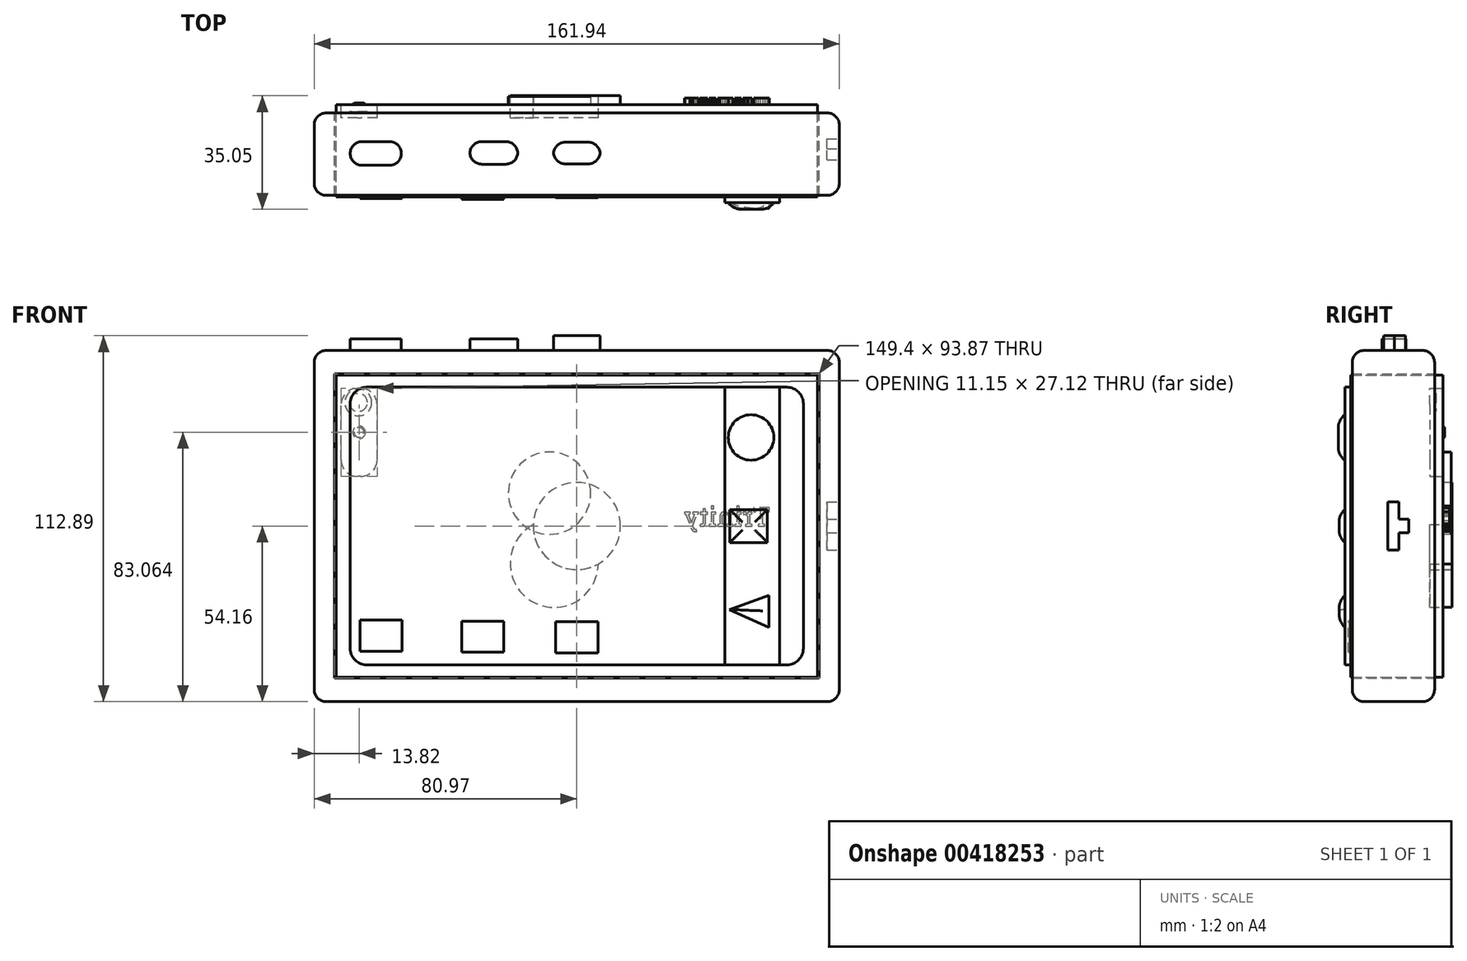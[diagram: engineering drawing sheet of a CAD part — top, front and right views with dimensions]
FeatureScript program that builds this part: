
annotation { "Feature Type Name" : "Feature", "Feature Type Description" : "" }
export const myFeature = defineFeature(function(context is Context, id is Id, definition is map)
    precondition{}
    {
        {
            var Q0;
            Q0=qCreatedBy(makeId("Front.planeOp"),FACE);
            var sketch = newSketch(context, id + "F0", { "sketchPlane" : qUnion([Q0])});
            skLineSegment(sketch, "E0.bottom", {"start": v(-80.97, 54.16) * mm, "end": v(80.97, 54.16) * mm});
            skLineSegment(sketch, "E0.top", {"start": v(-80.97, -54.16) * mm, "end": v(80.97, -54.16) * mm});
            skLineSegment(sketch, "E0.left", {"start": v(-80.97, 54.16) * mm, "end": v(-80.97, -54.16) * mm});
            skLineSegment(sketch, "E0.right", {"start": v(80.97, 54.16) * mm, "end": v(80.97, -54.16) * mm});
            skPoint(sketch, "E0.middle", {"position": v(0, 0) * mm});
            skLineSegment(sketch, "E1.bottom", {"start": v(-74.7, 46.93) * mm, "end": v(74.7, 46.93) * mm});
            skLineSegment(sketch, "E1.top", {"start": v(-74.7, -46.93) * mm, "end": v(74.7, -46.93) * mm});
            skLineSegment(sketch, "E1.left", {"start": v(-74.7, 46.93) * mm, "end": v(-74.7, -46.93) * mm});
            skLineSegment(sketch, "E1.right", {"start": v(74.7, 46.93) * mm, "end": v(74.7, -46.93) * mm});
            skLineSegment(sketch, "E2.bottom", {"start": v(-69.88, 42.84) * mm, "end": v(69.88, 42.84) * mm});
            skLineSegment(sketch, "E2.top", {"start": v(-69.88, -42.84) * mm, "end": v(69.88, -42.84) * mm});
            skLineSegment(sketch, "E2.left", {"start": v(-69.88, 42.84) * mm, "end": v(-69.88, -42.84) * mm});
            skLineSegment(sketch, "E2.right", {"start": v(69.88, 42.84) * mm, "end": v(69.88, -42.84) * mm});
            skSolve(sketch);
        }
        {
            var Q0;
            Q0=makeQuery(id+"F0.imprint","IMPRINT",FACE,{"disambiguationData":[TD([[makeQuery(id+"F0.imprint","IMPRINT",EDGE,{"derivedFrom":sQuery(id+"F0.wireOp",EDGE,"E2.bottom")}),-1.0]])]});
            var Q1;
            Q1=makeQuery(id+"F0.imprint","IMPRINT",FACE,{"disambiguationData":[TD([[makeQuery(id+"F0.imprint","IMPRINT",EDGE,{"derivedFrom":sQuery(id+"F0.wireOp",EDGE,"E0.bottom")}),-1.0]])]});
            extrude(context, id + "F1", {"entities" : qUnion([Q0, Q1]), "depth" : 25.4 * mm});
        }
        {
            var Q0;
            Q0=makeQuery(id+"F1.opExtrude","SWEPT_FACE",FACE,{"disambiguationData":[OSD([sQuery(id+"F0.wireOp",EDGE,"E0.right")])]});
            var Q1;
            Q1=makeQuery(id+"F1.opExtrude","SWEPT_FACE",FACE,{"disambiguationData":[OSD([sQuery(id+"F0.wireOp",EDGE,"E0.bottom")])]});
            var Q2;
            Q2=makeQuery(id+"F1.opExtrude","SWEPT_FACE",FACE,{"disambiguationData":[OSD([sQuery(id+"F0.wireOp",EDGE,"E0.left")])]});
            var Q3;
            Q3=makeQuery(id+"F1.opExtrude","SWEPT_FACE",FACE,{"disambiguationData":[OSD([sQuery(id+"F0.wireOp",EDGE,"E0.top")])]});
            fillet(context, id + "F2", {"entities" : qUnion([Q0, Q1, Q2, Q3]), "radius" : 3.68 * mm, "tangentPropagation" : true, "allowEdgeOverflow" : false});
        }
        {
            var Q0;
            Q0=makeQuery(id+"F1.opExtrude","SWEPT_EDGE",EDGE,{"disambiguationData":[OSD([sQuery(id+"F0.wireOp",EDGE,"E2.bottom"),sQuery(id+"F0.wireOp",EDGE,"E2.left")])]});
            var Q1;
            Q1=makeQuery(id+"F1.opExtrude","SWEPT_EDGE",EDGE,{"disambiguationData":[OSD([sQuery(id+"F0.wireOp",EDGE,"E2.top"),sQuery(id+"F0.wireOp",EDGE,"E2.left")])]});
            var Q2;
            Q2=makeQuery(id+"F1.opExtrude","SWEPT_EDGE",EDGE,{"disambiguationData":[OSD([sQuery(id+"F0.wireOp",EDGE,"E2.top"),sQuery(id+"F0.wireOp",EDGE,"E2.right")])]});
            var Q3;
            Q3=makeQuery(id+"F1.opExtrude","SWEPT_EDGE",EDGE,{"disambiguationData":[OSD([sQuery(id+"F0.wireOp",EDGE,"E2.bottom"),sQuery(id+"F0.wireOp",EDGE,"E2.right")])]});
            fillet(context, id + "F3", {"entities" : qUnion([Q0, Q1, Q2, Q3]), "radius" : 5.08 * mm, "tangentPropagation" : true, "allowEdgeOverflow" : false});
        }
        {
            var Q0;
            Q0=makeQuery(id+"F1.opExtrude","SWEPT_FACE",FACE,{"disambiguationData":[OSD([sQuery(id+"F0.wireOp",EDGE,"E0.bottom")])]});
            var sketch = newSketch(context, id + "F4", { "sketchPlane" : qUnion([Q0])});
            skLineSegment(sketch, "E3", {"start": v(-69.9, -16.15) * mm, "end": v(-54.1, -16.15) * mm});
            skLineSegment(sketch, "E4", {"start": v(-54.1, -16.15) * mm, "end": v(-54.1, -8.85) * mm});
            skLineSegment(sketch, "E5", {"start": v(-54.1, -8.85) * mm, "end": v(-69.9, -8.85) * mm});
            skLineSegment(sketch, "E6", {"start": v(-69.9, -8.85) * mm, "end": v(-69.9, -16.15) * mm});
            skSolve(sketch);
        }
        {
            var Q0;
            Q0=makeQuery(id+"F4.imprint","IMPRINT",FACE,{"disambiguationData":[TD([[makeQuery(id+"F4.imprint","IMPRINT",EDGE,{"derivedFrom":sQuery(id+"F4.wireOp",EDGE,"E3")}),1.0]])]});
            extrude(context, id + "F5", {"entities" : qUnion([Q0]), "operationType" : NewBodyOperationType.ADD, "depth" : 3.56 * mm});
        }
        {
            var Q0;
            Q0=makeQuery(id+"F1.opExtrude","CAP_FACE",FACE,{"disambiguationData":[OSD([sQuery(id+"F0.wireOp",EDGE,"E2.bottom"),sQuery(id+"F0.wireOp",EDGE,"E2.top"),sQuery(id+"F0.wireOp",EDGE,"E2.left"),sQuery(id+"F0.wireOp",EDGE,"E2.right")])],"isStart":true});
            var sketch = newSketch(context, id + "F6", { "sketchPlane" : qUnion([Q0])});
            skLineSegment(sketch, "E7.bottom", {"start": v(74.26, 46.6) * mm, "end": v(-74.26, 46.6) * mm});
            skLineSegment(sketch, "E7.top", {"start": v(74.26, -46.6) * mm, "end": v(-74.26, -46.6) * mm});
            skLineSegment(sketch, "E7.left", {"start": v(74.26, 46.6) * mm, "end": v(74.26, -46.6) * mm});
            skLineSegment(sketch, "E7.right", {"start": v(-74.26, 46.6) * mm, "end": v(-74.26, -46.6) * mm});
            skPoint(sketch, "E7.middle", {"position": v(0, 0) * mm});
            skSolve(sketch);
        }
        {
            var Q0;
            Q0=makeQuery(id+"F6.imprint","IMPRINT",FACE,{"disambiguationData":[TD([[makeQuery(id+"F6.imprint","IMPRINT",EDGE,{"derivedFrom":sQuery(id+"F6.wireOp",EDGE,"E7.bottom")}),1.0]])]});
            extrude(context, id + "F7", {"entities" : qUnion([Q0]), "operationType" : NewBodyOperationType.ADD, "oppositeDirection" : true, "depth" : 25.9 * mm});
        }
        {
            var Q0;
            Q0=makeQuery(id+"F5.opExtrude","SWEPT_EDGE",EDGE,{"disambiguationData":[OSD([sQuery(id+"F4.wireOp",EDGE,"E3"),sQuery(id+"F4.wireOp",EDGE,"E6")])]});
            var Q1;
            Q1=makeQuery(id+"F5.opExtrude","SWEPT_EDGE",EDGE,{"disambiguationData":[OSD([sQuery(id+"F4.wireOp",EDGE,"E5"),sQuery(id+"F4.wireOp",EDGE,"E6")])]});
            var Q2;
            Q2=makeQuery(id+"F5.opExtrude","SWEPT_EDGE",EDGE,{"disambiguationData":[OSD([sQuery(id+"F4.wireOp",EDGE,"E3"),sQuery(id+"F4.wireOp",EDGE,"E4")])]});
            var Q3;
            Q3=makeQuery(id+"F5.opExtrude","SWEPT_EDGE",EDGE,{"disambiguationData":[OSD([sQuery(id+"F4.wireOp",EDGE,"E4"),sQuery(id+"F4.wireOp",EDGE,"E5")])]});
            fillet(context, id + "F8", {"entities" : qUnion([Q0, Q1, Q2, Q3]), "radius" : 3.68 * mm, "tangentPropagation" : true, "allowEdgeOverflow" : false});
        }
        {
            var Q0;
            {var subQ0=sQuery(id+"F0.wireOp",EDGE,"E2.right");var subQ1=sQuery(id+"F0.wireOp",EDGE,"E2.left");var subQ2=sQuery(id+"F0.wireOp",EDGE,"E2.top");var subQ3=sQuery(id+"F0.wireOp",EDGE,"E2.bottom");Q0=makeQuery(id+"F7.boolean.opBoolean","MERGE",FACE,{"derivedFrom":[makeQuery(id+"F1.opExtrude","CAP_FACE",FACE,{"disambiguationData":[OSD([subQ3,subQ2,subQ1,subQ0])],"isStart":true}),makeQuery(id+"F7.opExtrude","CAP_FACE",FACE,{"disambiguationData":[OSD([subQ3,subQ2,subQ1,subQ0,sQuery(id+"F6.wireOp",EDGE,"E7.bottom"),sQuery(id+"F6.wireOp",EDGE,"E7.top"),sQuery(id+"F6.wireOp",EDGE,"E7.left"),sQuery(id+"F6.wireOp",EDGE,"E7.right")])],"isStart":true})]});}
            var sketch = newSketch(context, id + "F9", { "sketchPlane" : qUnion([Q0])});
            skLineSegment(sketch, "E8.bottom", {"start": v(74.26, 46.6) * mm, "end": v(-74.26, 46.6) * mm});
            skLineSegment(sketch, "E8.top", {"start": v(74.26, -46.6) * mm, "end": v(-74.26, -46.6) * mm});
            skLineSegment(sketch, "E8.left", {"start": v(74.26, 46.6) * mm, "end": v(74.26, -46.6) * mm});
            skLineSegment(sketch, "E8.right", {"start": v(-74.26, 46.6) * mm, "end": v(-74.26, -46.6) * mm});
            skPoint(sketch, "E8.middle", {"position": v(0, 0) * mm});
            skSolve(sketch);
        }
        {
            var Q0;
            Q0=makeQuery(id+"F9.imprint","IMPRINT",FACE,{"disambiguationData":[TD([[makeQuery(id+"F9.imprint","IMPRINT",EDGE,{"derivedFrom":sQuery(id+"F9.wireOp",EDGE,"E8.bottom")}),1.0]])]});
            extrude(context, id + "F10", {"entities" : qUnion([Q0]), "depth" : 2.54 * mm});
        }
        {
            var Q0;
            Q0=makeQuery(id+"F1.opExtrude","SWEPT_FACE",FACE,{"disambiguationData":[OSD([sQuery(id+"F0.wireOp",EDGE,"E0.bottom")])]});
            var sketch = newSketch(context, id + "F11", { "sketchPlane" : qUnion([Q0])});
            skLineSegment(sketch, "E9", {"start": v(-62, -12.33) * mm, "end": v(10.84, -12.33) * mm, "construction": true});
            skPoint(sketch, "E9.startSnap0", {"position": v(-62, -16.15) * mm});
            skLineSegment(sketch, "E10", {"start": v(10.84, -12.33) * mm, "end": v(77.28, -12.33) * mm, "construction": true});
            skLineSegment(sketch, "E11.bottom", {"start": v(-32.98, -15.8) * mm, "end": v(-18.19, -15.8) * mm});
            skLineSegment(sketch, "E11.top", {"start": v(-32.98, -8.85) * mm, "end": v(-18.19, -8.85) * mm});
            skLineSegment(sketch, "E11.left", {"start": v(-32.98, -15.8) * mm, "end": v(-32.98, -8.85) * mm});
            skLineSegment(sketch, "E11.right", {"start": v(-18.19, -15.8) * mm, "end": v(-18.19, -8.85) * mm});
            skPoint(sketch, "E11.middle", {"position": v(-25.58, -12.33) * mm});
            skSolve(sketch);
        }
        {
            var Q0;
            Q0=makeQuery(id+"F11.imprint","IMPRINT",FACE,{"disambiguationData":[TD([[makeQuery(id+"F11.imprint","IMPRINT",EDGE,{"derivedFrom":sQuery(id+"F11.wireOp",EDGE,"E11.bottom")}),1.0]])]});
            extrude(context, id + "F12", {"entities" : qUnion([Q0]), "operationType" : NewBodyOperationType.ADD, "depth" : 3.56 * mm});
        }
        {
            var Q0;
            Q0=makeQuery(id+"F12.opExtrude","SWEPT_EDGE",EDGE,{"disambiguationData":[OSD([sQuery(id+"F11.wireOp",EDGE,"E11.bottom"),sQuery(id+"F11.wireOp",EDGE,"E11.left")])]});
            var Q1;
            Q1=makeQuery(id+"F12.opExtrude","SWEPT_EDGE",EDGE,{"disambiguationData":[OSD([sQuery(id+"F11.wireOp",EDGE,"E11.top"),sQuery(id+"F11.wireOp",EDGE,"E11.left")])]});
            var Q2;
            Q2=makeQuery(id+"F12.opExtrude","SWEPT_EDGE",EDGE,{"disambiguationData":[OSD([sQuery(id+"F11.wireOp",EDGE,"E11.bottom"),sQuery(id+"F11.wireOp",EDGE,"E11.right")])]});
            var Q3;
            Q3=makeQuery(id+"F12.opExtrude","SWEPT_EDGE",EDGE,{"disambiguationData":[OSD([sQuery(id+"F11.wireOp",EDGE,"E11.top"),sQuery(id+"F11.wireOp",EDGE,"E11.right")])]});
            fillet(context, id + "F13", {"entities" : qUnion([Q0, Q1, Q2, Q3]), "radius" : 3.68 * mm, "tangentPropagation" : true, "allowEdgeOverflow" : false});
        }
        {
            var Q0;
            Q0=makeQuery(id+"F1.opExtrude","SWEPT_FACE",FACE,{"disambiguationData":[OSD([sQuery(id+"F0.wireOp",EDGE,"E0.bottom")])]});
            var sketch = newSketch(context, id + "F14", { "sketchPlane" : qUnion([Q0])});
            skLineSegment(sketch, "E12", {"start": v(-25.73, -12.36) * mm, "end": v(17.21, -12.36) * mm, "construction": true});
            skLineSegment(sketch, "E13.bottom", {"start": v(-7.2, -15.69) * mm, "end": v(7.2, -15.69) * mm});
            skLineSegment(sketch, "E13.top", {"start": v(-7.2, -9.03) * mm, "end": v(7.2, -9.03) * mm});
            skLineSegment(sketch, "E13.left", {"start": v(-7.2, -15.69) * mm, "end": v(-7.2, -9.03) * mm});
            skLineSegment(sketch, "E13.right", {"start": v(7.2, -15.69) * mm, "end": v(7.2, -9.03) * mm});
            skPoint(sketch, "E13.middle", {"position": v(0, -12.36) * mm});
            skSolve(sketch);
        }
        {
            var Q0;
            Q0=makeQuery(id+"F14.imprint","IMPRINT",FACE,{"disambiguationData":[TD([[makeQuery(id+"F14.imprint","IMPRINT",EDGE,{"derivedFrom":sQuery(id+"F14.wireOp",EDGE,"E13.bottom")}),1.0]])]});
            extrude(context, id + "F15", {"entities" : qUnion([Q0]), "operationType" : NewBodyOperationType.ADD, "depth" : 4.57 * mm});
        }
        {
            var Q0;
            Q0=makeQuery(id+"F15.opExtrude","SWEPT_EDGE",EDGE,{"disambiguationData":[OSD([sQuery(id+"F14.wireOp",EDGE,"E13.bottom"),sQuery(id+"F14.wireOp",EDGE,"E13.right")])]});
            var Q1;
            Q1=makeQuery(id+"F15.opExtrude","SWEPT_EDGE",EDGE,{"disambiguationData":[OSD([sQuery(id+"F14.wireOp",EDGE,"E13.top"),sQuery(id+"F14.wireOp",EDGE,"E13.right")])]});
            var Q2;
            Q2=makeQuery(id+"F15.opExtrude","SWEPT_EDGE",EDGE,{"disambiguationData":[OSD([sQuery(id+"F14.wireOp",EDGE,"E13.bottom"),sQuery(id+"F14.wireOp",EDGE,"E13.left")])]});
            var Q3;
            Q3=makeQuery(id+"F15.opExtrude","SWEPT_EDGE",EDGE,{"disambiguationData":[OSD([sQuery(id+"F14.wireOp",EDGE,"E13.top"),sQuery(id+"F14.wireOp",EDGE,"E13.left")])]});
            fillet(context, id + "F16", {"entities" : qUnion([Q0, Q1, Q2, Q3]), "radius" : 3.68 * mm, "tangentPropagation" : true, "allowEdgeOverflow" : false});
        }
        {
            var Q0;
            Q0=makeQuery(id+"F1.opExtrude","CAP_FACE",FACE,{"disambiguationData":[OSD([sQuery(id+"F0.wireOp",EDGE,"E2.bottom"),sQuery(id+"F0.wireOp",EDGE,"E2.top"),sQuery(id+"F0.wireOp",EDGE,"E2.left"),sQuery(id+"F0.wireOp",EDGE,"E2.right")])],"isStart":false});
            var sketch = newSketch(context, id + "F17", { "sketchPlane" : qUnion([Q0])});
            skLineSegment(sketch, "E14.bottom", {"start": v(-53.84, -29.05) * mm, "end": v(-66.85, -29.05) * mm});
            skLineSegment(sketch, "E14.top", {"start": v(-53.84, -38.68) * mm, "end": v(-66.85, -38.68) * mm});
            skLineSegment(sketch, "E14.left", {"start": v(-53.84, -29.05) * mm, "end": v(-53.84, -38.68) * mm});
            skLineSegment(sketch, "E14.right", {"start": v(-66.85, -29.05) * mm, "end": v(-66.85, -38.68) * mm});
            skPoint(sketch, "E14.middle", {"position": v(-60.35, -33.87) * mm});
            skSolve(sketch);
        }
        {
            var Q0;
            Q0=makeQuery(id+"F17.imprint","IMPRINT",FACE,{"disambiguationData":[TD([[makeQuery(id+"F17.imprint","IMPRINT",EDGE,{"derivedFrom":sQuery(id+"F17.wireOp",EDGE,"E14.bottom")}),1.0]])]});
            extrude(context, id + "F18", {"entities" : qUnion([Q0]), "depth" : 1.02 * mm});
        }
        {
            var Q0;
            Q0=makeQuery(id+"F1.opExtrude","CAP_FACE",FACE,{"disambiguationData":[OSD([sQuery(id+"F0.wireOp",EDGE,"E2.bottom"),sQuery(id+"F0.wireOp",EDGE,"E2.top"),sQuery(id+"F0.wireOp",EDGE,"E2.left"),sQuery(id+"F0.wireOp",EDGE,"E2.right")])],"isStart":false});
            var sketch = newSketch(context, id + "F19", { "sketchPlane" : qUnion([Q0])});
            skLineSegment(sketch, "E15", {"start": v(-62.3, -34.14) * mm, "end": v(15.58, -34.14) * mm, "construction": true});
            skLineSegment(sketch, "E16.bottom", {"start": v(-35.48, -38.96) * mm, "end": v(-22.47, -38.96) * mm});
            skLineSegment(sketch, "E16.top", {"start": v(-35.48, -29.32) * mm, "end": v(-22.47, -29.32) * mm});
            skLineSegment(sketch, "E16.left", {"start": v(-35.48, -38.96) * mm, "end": v(-35.48, -29.32) * mm});
            skLineSegment(sketch, "E16.right", {"start": v(-22.47, -38.96) * mm, "end": v(-22.47, -29.32) * mm});
            skPoint(sketch, "E16.middle", {"position": v(-28.98, -34.14) * mm});
            skSolve(sketch);
        }
        {
            var Q0;
            Q0=makeQuery(id+"F19.imprint","IMPRINT",FACE,{"disambiguationData":[TD([[makeQuery(id+"F19.imprint","IMPRINT",EDGE,{"derivedFrom":sQuery(id+"F19.wireOp",EDGE,"E16.bottom")}),1.0]])]});
            extrude(context, id + "F20", {"entities" : qUnion([Q0]), "depth" : 1.27 * mm});
        }
        {
            var Q0;
            Q0=makeQuery(id+"F1.opExtrude","CAP_FACE",FACE,{"disambiguationData":[OSD([sQuery(id+"F0.wireOp",EDGE,"E2.bottom"),sQuery(id+"F0.wireOp",EDGE,"E2.top"),sQuery(id+"F0.wireOp",EDGE,"E2.left"),sQuery(id+"F0.wireOp",EDGE,"E2.right")])],"isStart":false});
            var sketch = newSketch(context, id + "F21", { "sketchPlane" : qUnion([Q0])});
            skLineSegment(sketch, "E17", {"start": v(-28.88, -34.33) * mm, "end": v(69.88, -34.33) * mm, "construction": true});
            skLineSegment(sketch, "E18.bottom", {"start": v(-6.5, -39.15) * mm, "end": v(6.5, -39.15) * mm});
            skLineSegment(sketch, "E18.top", {"start": v(-6.5, -29.5) * mm, "end": v(6.5, -29.5) * mm});
            skLineSegment(sketch, "E18.left", {"start": v(-6.5, -39.15) * mm, "end": v(-6.5, -29.5) * mm});
            skLineSegment(sketch, "E18.right", {"start": v(6.5, -39.15) * mm, "end": v(6.5, -29.5) * mm});
            skPoint(sketch, "E18.middle", {"position": v(0, -34.33) * mm});
            skSolve(sketch);
        }
        {
            var Q0;
            Q0=makeQuery(id+"F21.imprint","IMPRINT",FACE,{"disambiguationData":[TD([[makeQuery(id+"F21.imprint","IMPRINT",EDGE,{"derivedFrom":sQuery(id+"F21.wireOp",EDGE,"E18.bottom")}),1.0]])]});
            extrude(context, id + "F22", {"entities" : qUnion([Q0]), "depth" : 0.76 * mm});
        }
        {
            var Q0;
            Q0=makeQuery(id+"F1.opExtrude","CAP_FACE",FACE,{"disambiguationData":[OSD([sQuery(id+"F0.wireOp",EDGE,"E2.bottom"),sQuery(id+"F0.wireOp",EDGE,"E2.top"),sQuery(id+"F0.wireOp",EDGE,"E2.left"),sQuery(id+"F0.wireOp",EDGE,"E2.right")])],"isStart":false});
            var sketch = newSketch(context, id + "F23", { "sketchPlane" : qUnion([Q0])});
            skLineSegment(sketch, "E19.bottom", {"start": v(45.66, -42.84) * mm, "end": v(62.53, -42.84) * mm});
            skLineSegment(sketch, "E19.top", {"start": v(45.66, 42.84) * mm, "end": v(62.53, 42.84) * mm});
            skLineSegment(sketch, "E19.left", {"start": v(45.66, -42.84) * mm, "end": v(45.66, 42.84) * mm});
            skLineSegment(sketch, "E19.right", {"start": v(62.53, -42.84) * mm, "end": v(62.53, 42.84) * mm});
            skPoint(sketch, "E19.middle", {"position": v(54.1, 0) * mm});
            skSolve(sketch);
        }
        {
            var Q0;
            Q0=makeQuery(id+"F23.imprint","IMPRINT",FACE,{"disambiguationData":[TD([[makeQuery(id+"F23.imprint","IMPRINT",EDGE,{"derivedFrom":sQuery(id+"F23.wireOp",EDGE,"E19.bottom")}),1.0]])]});
            extrude(context, id + "F24", {"entities" : qUnion([Q0]), "depth" : 2.3 * mm});
        }
        {
            var Q0;
            Q0=makeQuery(id+"F24.opExtrude","CAP_FACE",FACE,{"disambiguationData":[OSD([sQuery(id+"F23.wireOp",EDGE,"E19.bottom"),sQuery(id+"F23.wireOp",EDGE,"E19.top"),sQuery(id+"F23.wireOp",EDGE,"E19.left"),sQuery(id+"F23.wireOp",EDGE,"E19.right")])],"isStart":false});
            var sketch = newSketch(context, id + "F25", { "sketchPlane" : qUnion([Q0])});
            skLineSegment(sketch, "E20.bottom", {"start": v(58.8, 5.06) * mm, "end": v(47.23, 5.06) * mm});
            skLineSegment(sketch, "E20.top", {"start": v(58.8, -5.06) * mm, "end": v(47.23, -5.06) * mm});
            skLineSegment(sketch, "E20.left", {"start": v(58.8, 5.06) * mm, "end": v(58.8, -5.06) * mm});
            skLineSegment(sketch, "E20.right", {"start": v(47.23, 5.06) * mm, "end": v(47.23, -5.06) * mm});
            skPoint(sketch, "E20.middle", {"position": v(53.01, 0) * mm});
            skSolve(sketch);
        }
        {
            var Q0;
            Q0=makeQuery(id+"F25.imprint","IMPRINT",FACE,{"disambiguationData":[TD([[makeQuery(id+"F25.imprint","IMPRINT",EDGE,{"derivedFrom":sQuery(id+"F25.wireOp",EDGE,"E20.bottom")}),1.0]])]});
            extrude(context, id + "F26", {"entities" : qUnion([Q0]), "depth" : 1.78 * mm});
        }
        {
            var Q0;
            Q0=makeQuery(id+"F24.opExtrude","CAP_FACE",FACE,{"disambiguationData":[OSD([sQuery(id+"F23.wireOp",EDGE,"E19.bottom"),sQuery(id+"F23.wireOp",EDGE,"E19.top"),sQuery(id+"F23.wireOp",EDGE,"E19.left"),sQuery(id+"F23.wireOp",EDGE,"E19.right")])],"isStart":false});
            var sketch = newSketch(context, id + "F27", { "sketchPlane" : qUnion([Q0])});
            skLineSegment(sketch, "E21", {"start": v(53.75, 0) * mm, "end": v(53.75, -42.84) * mm, "construction": true});
            skPoint(sketch, "E21.startSnap0", {"position": v(62.53, 0) * mm});
            skLineSegment(sketch, "E22", {"start": v(53.75, 0) * mm, "end": v(53.75, 42.84) * mm, "construction": true});
            skCircle(sketch, "E23", {"center": v(53.75, 27.32) * mm, "radius": 7.02 * mm});
            skSolve(sketch);
        }
        {
            var Q0;
            Q0=makeQuery(id+"F27.imprint","IMPRINT",FACE,{"disambiguationData":[TD([[makeQuery(id+"F27.imprint","IMPRINT",EDGE,{"derivedFrom":sQuery(id+"F27.wireOp",EDGE,"E23")}),1.0]])]});
            extrude(context, id + "F28", {"entities" : qUnion([Q0]), "depth" : 2.03 * mm});
        }
        {
            var Q0;
            Q0=makeQuery(id+"F24.opExtrude","CAP_FACE",FACE,{"disambiguationData":[OSD([sQuery(id+"F23.wireOp",EDGE,"E19.bottom"),sQuery(id+"F23.wireOp",EDGE,"E19.top"),sQuery(id+"F23.wireOp",EDGE,"E19.left"),sQuery(id+"F23.wireOp",EDGE,"E19.right")])],"isStart":false});
            var sketch = newSketch(context, id + "F29", { "sketchPlane" : qUnion([Q0])});
            skLineSegment(sketch, "E24", {"start": v(53.96, 0) * mm, "end": v(53.96, -42.84) * mm, "construction": true});
            skLineSegment(sketch, "E25", {"start": v(47.07, -25.76) * mm, "end": v(59.23, -21.42) * mm});
            skPoint(sketch, "E25.endSnap0", {"position": v(53.96, -21.42) * mm});
            skLineSegment(sketch, "E26", {"start": v(59.23, -21.42) * mm, "end": v(59.23, -31.23) * mm});
            skLineSegment(sketch, "E27", {"start": v(59.23, -31.23) * mm, "end": v(47.07, -25.76) * mm});
            skSolve(sketch);
        }
        {
            var Q0;
            Q0=makeQuery(id+"F29.imprint","IMPRINT",FACE,{"disambiguationData":[TD([[makeQuery(id+"F29.imprint","IMPRINT",EDGE,{"derivedFrom":sQuery(id+"F29.wireOp",EDGE,"E25")}),-1.0]])]});
            extrude(context, id + "F30", {"entities" : qUnion([Q0]), "depth" : 1.78 * mm});
        }
        {
            var Q0;
            Q0=makeQuery(id+"F10.opExtrude","CAP_FACE",FACE,{"disambiguationData":[OSD([sQuery(id+"F9.wireOp",EDGE,"E8.bottom"),sQuery(id+"F9.wireOp",EDGE,"E8.top"),sQuery(id+"F9.wireOp",EDGE,"E8.left"),sQuery(id+"F9.wireOp",EDGE,"E8.right")])],"isStart":false});
            var sketch = newSketch(context, id + "F31", { "sketchPlane" : qUnion([Q0])});
            skCircle(sketch, "E28", {"center": v(0, 0) * mm, "radius": 13.44 * mm});
            skSolve(sketch);
        }
        {
            var Q0;
            Q0=makeQuery(id+"F31.imprint","IMPRINT",FACE,{"disambiguationData":[TD([[makeQuery(id+"F31.imprint","IMPRINT",EDGE,{"derivedFrom":sQuery(id+"F31.wireOp",EDGE,"E28")}),1.0]])]});
            extrude(context, id + "F32", {"entities" : qUnion([Q0]), "depth" : 2.8 * mm});
        }
        {
            var Q0;
            Q0=makeQuery(id+"F10.opExtrude","CAP_FACE",FACE,{"disambiguationData":[OSD([sQuery(id+"F9.wireOp",EDGE,"E8.bottom"),sQuery(id+"F9.wireOp",EDGE,"E8.top"),sQuery(id+"F9.wireOp",EDGE,"E8.left"),sQuery(id+"F9.wireOp",EDGE,"E8.right")])],"isStart":false});
            var sketch = newSketch(context, id + "F33", { "sketchPlane" : qUnion([Q0])});
            skCircle(sketch, "E29", {"center": v(8.4, 10.13) * mm, "radius": 12.7 * mm});
            skSolve(sketch);
        }
        {
            var Q0;
            Q0=makeQuery(id+"F33.imprint","IMPRINT",FACE,{"disambiguationData":[TD([[makeQuery(id+"F33.imprint","IMPRINT",EDGE,{"derivedFrom":sQuery(id+"F33.wireOp",EDGE,"E29")}),1.0]])]});
            extrude(context, id + "F34", {"entities" : qUnion([Q0]), "depth" : 2.54 * mm});
        }
        {
            var Q0;
            Q0=makeQuery(id+"F32.opExtrude","CAP_FACE",FACE,{"disambiguationData":[OSD([sQuery(id+"F31.wireOp",EDGE,"E28")])],"isStart":false});
            var sketch = newSketch(context, id + "F35", { "sketchPlane" : qUnion([Q0])});
            skCircle(sketch, "E30", {"center": v(6.96, -11.5) * mm, "radius": 13.6 * mm});
            skSolve(sketch);
        }
        {
            var Q0;
            {var subQ0=sQuery(id+"F35.wireOp",EDGE,"E30");var subQ1=makeQuery(id+"F32.opExtrude","CAP_EDGE",EDGE,{"disambiguationData":[OSD([sQuery(id+"F31.wireOp",EDGE,"E28")])],"isStart":false});var subQ2=makeQuery(id+"F35.imprint","INTERSECT",VERTEX,{"disambiguationData":[OD(0.0)],"derivedFrom":[subQ1,subQ0]});Q0=makeQuery(id+"F35.imprint","IMPRINT",FACE,{"disambiguationData":[TD([[makeQuery(id+"F35.imprint","IMPRINT",EDGE,{"disambiguationData":[TD([[subQ2,1.0]])],"derivedFrom":subQ0}),1.0]])]});}
            extrude(context, id + "F36", {"entities" : qUnion([Q0]), "oppositeDirection" : true, "depth" : 6.86 * mm});
        }
        {
            var Q0;
            Q0=makeQuery(id+"F10.opExtrude","CAP_FACE",FACE,{"disambiguationData":[OSD([sQuery(id+"F9.wireOp",EDGE,"E8.bottom"),sQuery(id+"F9.wireOp",EDGE,"E8.top"),sQuery(id+"F9.wireOp",EDGE,"E8.left"),sQuery(id+"F9.wireOp",EDGE,"E8.right")])],"isStart":false});
            var sketch = newSketch(context, id + "F37", { "sketchPlane" : qUnion([Q0])});
            skText(sketch, "E31", { "text": "Trinity", "fontName": "RobotoSlab-Regular.ttf"});
            const initialGuessF37  = {"E31": [-0.05947, 0, 1, 0, 0.0058]};
            skSetInitialGuess(sketch, initialGuessF37);
            skSolve(sketch);
        }
        {
            var Q0;
            Q0 = qSketchRegion(id + "F37", true);
            extrude(context, id + "F38", {"entities" : qUnion([Q0]), "depth" : 2.03 * mm});
        }
        {
            var Q0;
            Q0=makeQuery(id+"F30.opExtrude","CAP_EDGE",EDGE,{"disambiguationData":[OSD([sQuery(id+"F29.wireOp",EDGE,"E27")])],"isStart":false});
            var Q1;
            Q1=makeQuery(id+"F30.opExtrude","CAP_EDGE",EDGE,{"disambiguationData":[OSD([sQuery(id+"F29.wireOp",EDGE,"E25")])],"isStart":false});
            var Q2;
            Q2=makeQuery(id+"F26.opExtrude","CAP_EDGE",EDGE,{"disambiguationData":[OSD([sQuery(id+"F25.wireOp",EDGE,"E20.right")])],"isStart":false});
            var Q3;
            Q3=makeQuery(id+"F26.opExtrude","CAP_EDGE",EDGE,{"disambiguationData":[OSD([sQuery(id+"F25.wireOp",EDGE,"E20.bottom")])],"isStart":false});
            var Q4;
            Q4=makeQuery(id+"F26.opExtrude","CAP_EDGE",EDGE,{"disambiguationData":[OSD([sQuery(id+"F25.wireOp",EDGE,"E20.left")])],"isStart":false});
            var Q5;
            Q5=makeQuery(id+"F26.opExtrude","CAP_EDGE",EDGE,{"disambiguationData":[OSD([sQuery(id+"F25.wireOp",EDGE,"E20.top")])],"isStart":false});
            var Q6;
            Q6=makeQuery(id+"F28.opExtrude","CAP_FACE",FACE,{"disambiguationData":[OSD([sQuery(id+"F27.wireOp",EDGE,"E23")])],"isStart":false});
            fillet(context, id + "F39", {"entities" : qUnion([Q0, Q1, Q2, Q3, Q4, Q5, Q6]), "radius" : 5.08 * mm, "tangentPropagation" : true, "allowEdgeOverflow" : false});
        }
        {
            var Q0;
            Q0=makeQuery(id+"F1.opExtrude","SWEPT_FACE",FACE,{"disambiguationData":[OSD([sQuery(id+"F0.wireOp",EDGE,"E0.right")])]});
            var sketch = newSketch(context, id + "F40", { "sketchPlane" : qUnion([Q0])});
            skLineSegment(sketch, "E32", {"start": v(-21.72, 0) * mm, "end": v(0, 0) * mm, "construction": true});
            skLineSegment(sketch, "E33", {"start": v(-14.5, 0) * mm, "end": v(-14.5, -7.44) * mm});
            skLineSegment(sketch, "E34", {"start": v(-14.5, -7.44) * mm, "end": v(-11.01, -7.44) * mm});
            skLineSegment(sketch, "E35", {"start": v(-11.01, -7.44) * mm, "end": v(-11.01, -2.11) * mm});
            skLineSegment(sketch, "E36", {"start": v(-11.01, -2.11) * mm, "end": v(-7.94, -2.11) * mm});
            skLineSegment(sketch, "E37", {"start": v(-7.94, -2.11) * mm, "end": v(-7.94, 2.11) * mm});
            skLineSegment(sketch, "E38", {"start": v(-7.94, 2.11) * mm, "end": v(-11.01, 2.11) * mm});
            skLineSegment(sketch, "E39", {"start": v(-11.01, 2.11) * mm, "end": v(-11.01, 7.44) * mm});
            skLineSegment(sketch, "E40", {"start": v(-11.01, 7.44) * mm, "end": v(-14.5, 7.44) * mm});
            skLineSegment(sketch, "E41", {"start": v(-14.5, 7.44) * mm, "end": v(-14.5, 0) * mm});
            skSolve(sketch);
        }
        {
            var Q0;
            Q0=makeQuery(id+"F40.imprint","IMPRINT",FACE,{"disambiguationData":[TD([[makeQuery(id+"F40.imprint","IMPRINT",EDGE,{"derivedFrom":sQuery(id+"F40.wireOp",EDGE,"E33")}),1.0]])]});
            extrude(context, id + "F41", {"entities" : qUnion([Q0]), "operationType" : NewBodyOperationType.REMOVE, "oppositeDirection" : true, "depth" : 3.8 * mm});
        }
        {
            var Q0;
            Q0=makeQuery(id+"F10.opExtrude","CAP_FACE",FACE,{"disambiguationData":[OSD([sQuery(id+"F9.wireOp",EDGE,"E8.bottom"),sQuery(id+"F9.wireOp",EDGE,"E8.top"),sQuery(id+"F9.wireOp",EDGE,"E8.left"),sQuery(id+"F9.wireOp",EDGE,"E8.right")])],"isStart":false});
            var sketch = newSketch(context, id + "F42", { "sketchPlane" : qUnion([Q0])});
            skLineSegment(sketch, "E42.bottom", {"start": v(72.73, 42.46) * mm, "end": v(61.57, 42.46) * mm});
            skLineSegment(sketch, "E42.top", {"start": v(72.73, 15.34) * mm, "end": v(61.57, 15.34) * mm});
            skLineSegment(sketch, "E42.left", {"start": v(72.73, 42.46) * mm, "end": v(72.73, 15.34) * mm});
            skLineSegment(sketch, "E42.right", {"start": v(61.57, 42.46) * mm, "end": v(61.57, 15.34) * mm});
            skSolve(sketch);
        }
        {
            var Q0;
            Q0=makeQuery(id+"F42.imprint","IMPRINT",FACE,{"disambiguationData":[TD([[makeQuery(id+"F42.imprint","IMPRINT",EDGE,{"derivedFrom":sQuery(id+"F42.wireOp",EDGE,"E42.bottom")}),1.0]])]});
            extrude(context, id + "F43", {"entities" : qUnion([Q0]), "operationType" : NewBodyOperationType.REMOVE, "oppositeDirection" : true, "depth" : 4.06 * mm});
        }
        {
            var Q0;
            Q0=makeQuery(id+"F43.boolean.opBoolean","COPY",EDGE,{"derivedFrom":makeQuery(id+"F43.opExtrude","SWEPT_EDGE",EDGE,{"disambiguationData":[OSD([sQuery(id+"F42.wireOp",EDGE,"E42.bottom"),sQuery(id+"F42.wireOp",EDGE,"E42.left")])]})});
            var Q1;
            Q1=makeQuery(id+"F43.boolean.opBoolean","COPY",EDGE,{"derivedFrom":makeQuery(id+"F43.opExtrude","SWEPT_EDGE",EDGE,{"disambiguationData":[OSD([sQuery(id+"F42.wireOp",EDGE,"E42.bottom"),sQuery(id+"F42.wireOp",EDGE,"E42.right")])]})});
            var Q2;
            Q2=makeQuery(id+"F43.boolean.opBoolean","COPY",EDGE,{"derivedFrom":makeQuery(id+"F43.opExtrude","SWEPT_EDGE",EDGE,{"disambiguationData":[OSD([sQuery(id+"F42.wireOp",EDGE,"E42.top"),sQuery(id+"F42.wireOp",EDGE,"E42.left")])]})});
            var Q3;
            Q3=makeQuery(id+"F43.boolean.opBoolean","COPY",EDGE,{"derivedFrom":makeQuery(id+"F43.opExtrude","SWEPT_EDGE",EDGE,{"disambiguationData":[OSD([sQuery(id+"F42.wireOp",EDGE,"E42.top"),sQuery(id+"F42.wireOp",EDGE,"E42.right")])]})});
            fillet(context, id + "F44", {"entities" : qUnion([Q0, Q1, Q2, Q3]), "radius" : 5.08 * mm, "tangentPropagation" : true, "allowEdgeOverflow" : false});
        }
        {
            var Q0;
            {var subQ0=sQuery(id+"F0.wireOp",EDGE,"E2.right");var subQ1=sQuery(id+"F0.wireOp",EDGE,"E2.left");var subQ2=sQuery(id+"F0.wireOp",EDGE,"E2.top");var subQ3=sQuery(id+"F0.wireOp",EDGE,"E2.bottom");Q0=makeQuery(id+"F7.boolean.opBoolean","MERGE",FACE,{"derivedFrom":[makeQuery(id+"F1.opExtrude","CAP_FACE",FACE,{"disambiguationData":[OSD([subQ3,subQ2,subQ1,subQ0])],"isStart":true}),makeQuery(id+"F7.opExtrude","CAP_FACE",FACE,{"disambiguationData":[OSD([subQ3,subQ2,subQ1,subQ0,sQuery(id+"F6.wireOp",EDGE,"E7.bottom"),sQuery(id+"F6.wireOp",EDGE,"E7.top"),sQuery(id+"F6.wireOp",EDGE,"E7.left"),sQuery(id+"F6.wireOp",EDGE,"E7.right")])],"isStart":true})]});}
            var sketch = newSketch(context, id + "F45", { "sketchPlane" : qUnion([Q0])});
            skCircle(sketch, "E43", {"center": v(67.4, 38.13) * mm, "radius": 4.15 * mm});
            skSolve(sketch);
        }
        {
            var Q0;
            Q0=makeQuery(id+"F45.imprint","IMPRINT",FACE,{"disambiguationData":[TD([[makeQuery(id+"F45.imprint","IMPRINT",EDGE,{"derivedFrom":sQuery(id+"F45.wireOp",EDGE,"E43")}),1.0]])]});
            extrude(context, id + "F46", {"entities" : qUnion([Q0]), "depth" : 0.15 * mm});
        }
        {
            var Q0;
            Q0=makeQuery(id+"F46.opExtrude","CAP_FACE",FACE,{"disambiguationData":[OSD([sQuery(id+"F45.wireOp",EDGE,"E43")])],"isStart":false});
            var sketch = newSketch(context, id + "F47", { "sketchPlane" : qUnion([Q0])});
            skCircle(sketch, "E44", {"center": v(67.4, 38.13) * mm, "radius": 2.8 * mm});
            skSolve(sketch);
        }
        {
            var Q0;
            Q0=makeQuery(id+"F47.imprint","IMPRINT",FACE,{"disambiguationData":[TD([[makeQuery(id+"F47.imprint","IMPRINT",EDGE,{"derivedFrom":sQuery(id+"F47.wireOp",EDGE,"E44")}),1.0]])]});
            extrude(context, id + "F48", {"entities" : qUnion([Q0]), "depth" : 0.25 * mm});
        }
        {
            var Q0;
            Q0=makeQuery(id+"F10.opExtrude","CAP_FACE",FACE,{"disambiguationData":[OSD([sQuery(id+"F9.wireOp",EDGE,"E8.bottom"),sQuery(id+"F9.wireOp",EDGE,"E8.top"),sQuery(id+"F9.wireOp",EDGE,"E8.left"),sQuery(id+"F9.wireOp",EDGE,"E8.right")])],"isStart":false});
            var sketch = newSketch(context, id + "F49", { "sketchPlane" : qUnion([Q0])});
            skLineSegment(sketch, "E45", {"start": v(61.57, 28.9) * mm, "end": v(72.73, 28.9) * mm, "construction": true});
            skCircle(sketch, "E46", {"center": v(67.15, 28.9) * mm, "radius": 1.94 * mm});
            skSolve(sketch);
        }
        {
            var Q0;
            Q0=makeQuery(id+"F49.imprint","IMPRINT",FACE,{"disambiguationData":[TD([[makeQuery(id+"F49.imprint","IMPRINT",EDGE,{"derivedFrom":sQuery(id+"F49.wireOp",EDGE,"E46")}),1.0]])]});
            extrude(context, id + "F50", {"entities" : qUnion([Q0]), "depth" : 0.25 * mm});
        }
        {
            var Q0;
            Q0=makeQuery(id+"F50.opExtrude","CAP_FACE",FACE,{"disambiguationData":[OSD([sQuery(id+"F49.wireOp",EDGE,"E46")])],"isStart":false});
            var sketch = newSketch(context, id + "F51", { "sketchPlane" : qUnion([Q0])});
            skCircle(sketch, "E47", {"center": v(67.15, 28.9) * mm, "radius": 1.52 * mm});
            skSolve(sketch);
        }
        {
            var Q0;
            Q0=makeQuery(id+"F51.imprint","IMPRINT",FACE,{"disambiguationData":[TD([[makeQuery(id+"F51.imprint","IMPRINT",EDGE,{"derivedFrom":sQuery(id+"F51.wireOp",EDGE,"E47")}),1.0]])]});
            extrude(context, id + "F52", {"entities" : qUnion([Q0]), "depth" : 0.25 * mm});
        }
    });
